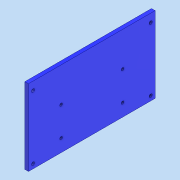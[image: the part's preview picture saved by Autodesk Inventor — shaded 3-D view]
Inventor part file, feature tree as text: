
AUTODESK INVENTOR PART (.ipt)
format: ipt  version: 2022 (Build 260153000, 153)  size: 115,200 bytes
history: native  units: mm
features: extrude x2, sketch x2
ambient origin geometry x8: Origin, YZ Plane, XZ Plane, XY Plane, X Axis, Y Axis, Z Axis, Center Point
bodies: Solid1 (feature_tree)
feature tree (4):
  extrude  "Extrusion1"  Depth=140.0mm
  extrude  "Extrusion2"  Depth=4.0mm
  sketch  "Sketch1"  dims[d0=84.0mm d1=140.0mm]
  sketch  "Sketch2"  dims[d2=3.5mm d3=5.0mm d4=5.0mm d5=3.5mm d6=9.0mm d7=5.0mm d8=4.0mm d9=0.0mm d10=36.0mm d11=32.0mm d12=14.0mm d13=3.0mm d14=3.0mm d15=3.0mm d16=3.0mm d17=4.0mm d18=0.0mm]
